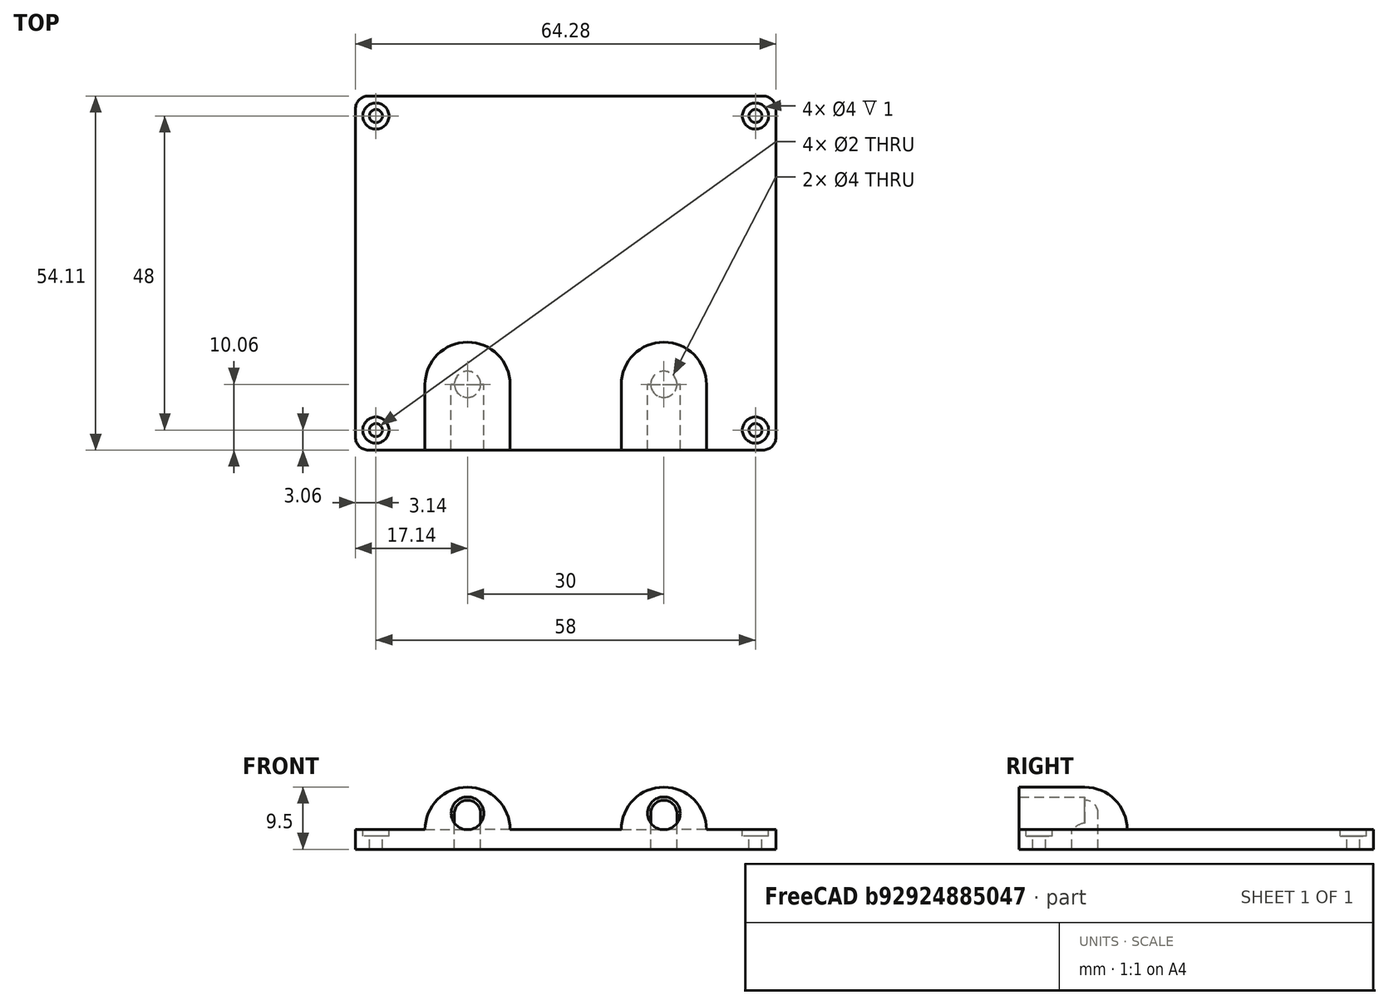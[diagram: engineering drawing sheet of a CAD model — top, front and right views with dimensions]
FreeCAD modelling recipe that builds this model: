
FCSTD DOCUMENT  (FreeCAD 0.19R24276 (Git))
Label: enclosureBack
License: All rights reserved
LicenseURL: http://en.wikipedia.org/wiki/All_rights_reserved
objects: Part::Cylinder×14, Part::MultiFuse×13, Part::Cut×4, Part::Sphere×4, Part::Box×3, Spreadsheet::Sheet×1, Part::Fillet×1
note: 39 computed .brp shape members not serialized (recipe doc carries the construction recipe); baked Part::Feature solids carry a one-line shape summary decoded from their .brp

FEATURE [Spreadsheet::Sheet] Spreadsheet  label="data"
  cells = A4=hole_dia; B4(hole_dia)==1.5mm; A5=standoff_dia; B5(standoff_dia)==4mm; A6=standoff_height; B6(standoff_height)==8mm; A7=case_standoff_dia; B7(case_standoff_dia)==5mm; A8=wall_thickness; B8(wall_thickness)==3mm; A9=case_thickness; B9(case_thickness)==15mm; A10=case_inner_width; B10(case_inner_width)==2.55in - 0.5mm; A11=case_inner_height; B11(case_inner_height)==2.15in - 0.5mm; A12=post_dia; B12(post_dia)==5mm; A13=post_depth; B13(post_depth)==10mm
FEATURE [Part::Box] Box  label="Cube"
  AttacherType = Attacher::AttachEngine3D
  Height = 3
  Length = 64.27
  Placement = pos=(-32.135,-27.055,0) rot=(0,0,1;0rad)
  Width = 54.11
  expr: Length = <<data>>.case_inner_width
  expr: Width = <<data>>.case_inner_height
  expr: .Placement.Base.y = -<<data>>.case_inner_height / 2
  expr: .Placement.Base.x = -<<data>>.case_inner_width / 2
  expr: Height = <<data>>.wall_thickness
FEATURE [Part::Fillet] Fillet
  Base = -> Box
  Edges = 4 edges r=2: [Edge1,Edge3,Edge5,Edge7]
FEATURE [Part::Cylinder] Cylinder
  Angle = 360
  AttacherType = Attacher::AttachEngine3D
  Height = 2
  Placement = pos=(0,0,2) rot=(0,0,1;0rad)
  Radius = 2
FEATURE [Part::Cylinder] Cylinder001
  Angle = 360
  AttacherType = Attacher::AttachEngine3D
  Height = 10
  Radius = 1
FEATURE [Part::MultiFuse] Fusion  label="screwHole"
  Placement = pos=(29,24,0) rot=(0,0,1;0rad)
  Shapes = -> [Cylinder001,Cylinder]
FEATURE [Part::Cylinder] Cylinder002
  Angle = 360
  AttacherType = Attacher::AttachEngine3D
  Height = 2
  Placement = pos=(0,0,2) rot=(0,0,1;0rad)
  Radius = 2
FEATURE [Part::Cylinder] Cylinder003
  Angle = 360
  AttacherType = Attacher::AttachEngine3D
  Height = 10
  Radius = 1
FEATURE [Part::MultiFuse] Fusion006  label="screwHole001"
  Placement = pos=(-29,24,0) rot=(0,0,1;0rad)
  Shapes = -> [Cylinder003,Cylinder002]
FEATURE [Part::Cylinder] Cylinder004
  Angle = 360
  AttacherType = Attacher::AttachEngine3D
  Height = 2
  Placement = pos=(0,0,2) rot=(0,0,1;0rad)
  Radius = 2
FEATURE [Part::Cylinder] Cylinder005
  Angle = 360
  AttacherType = Attacher::AttachEngine3D
  Height = 10
  Radius = 1
FEATURE [Part::MultiFuse] Fusion007  label="screwHole002"
  Placement = pos=(29,-24,0) rot=(0,0,1;0rad)
  Shapes = -> [Cylinder005,Cylinder004]
FEATURE [Part::Cylinder] Cylinder006
  Angle = 360
  AttacherType = Attacher::AttachEngine3D
  Height = 2
  Placement = pos=(0,0,2) rot=(0,0,1;0rad)
  Radius = 2
FEATURE [Part::Cylinder] Cylinder007
  Angle = 360
  AttacherType = Attacher::AttachEngine3D
  Height = 10
  Radius = 1
FEATURE [Part::MultiFuse] Fusion008  label="screwHole003"
  Placement = pos=(-29,-24,0) rot=(0,0,1;0rad)
  Shapes = -> [Cylinder007,Cylinder006]
FEATURE [Part::MultiFuse] Fusion009  label="ScrewHoles"
  Shapes = -> [Fusion008,Fusion,Fusion006,Fusion007]
FEATURE [Part::Cut] Cut
  Base = -> Fillet
  Tool = -> Fusion009
FEATURE [Part::Cylinder] Cylinder008
  Angle = 360
  AttacherType = Attacher::AttachEngine3D
  Height = 10
  Radius = 6.5
  expr: Height = <<data>>.post_depth
FEATURE [Part::Sphere] Sphere
  Angle1 = -90
  Angle2 = 90
  Angle3 = 360
  AttacherType = Attacher::AttachEngine3D
  Placement = pos=(0,0,10) rot=(0,0,1;0rad)
  Radius = 6.5
FEATURE [Part::Box] Box001  label="Cube001"
  AttacherType = Attacher::AttachEngine3D
  Height = 31
  Length = 16
  Placement = pos=(-8,0,0) rot=(0,0,1;0rad)
  Width = 10
FEATURE [Part::MultiFuse] Fusion010
  Shapes = -> [Sphere,Cylinder008]
FEATURE [Part::Cylinder] Cylinder009
  Angle = 360
  AttacherType = Attacher::AttachEngine3D
  Height = 10
  Placement = pos=(0,-2.5,0) rot=(0,0,1;0rad)
  Radius = 2.5
  expr: .Placement.Base.y = -<<data>>.post_dia / 2
  expr: Height = <<data>>.post_depth
  expr: Radius = <<data>>.post_dia / 2
FEATURE [Part::MultiFuse] Fusion011
  Shapes = -> [Cylinder009,Box001]
FEATURE [Part::Cut] Cut001  label="Hump"
  Base = -> Fusion010
  Placement = pos=(-15,-27.055,3) rot=(-1,0,0;1.5708rad)
  Tool = -> Fusion011
  expr: .Placement.Base.y = -<<data>>.case_inner_height / 2
  expr: .Placement.Base.z = <<data>>.wall_thickness
FEATURE [Part::Cylinder] Cylinder010
  Angle = 360
  AttacherType = Attacher::AttachEngine3D
  Height = 10
  Placement = pos=(0,-2.5,0) rot=(0,0,1;0rad)
  Radius = 2.5
  expr: Radius = <<data>>.post_dia / 2
  expr: Height = <<data>>.post_depth
  expr: .Placement.Base.y = -<<data>>.post_dia / 2
FEATURE [Part::Box] Box002  label="Cube002"
  AttacherType = Attacher::AttachEngine3D
  Height = 31
  Length = 16
  Placement = pos=(-8,0,0) rot=(0,0,1;0rad)
  Width = 10
FEATURE [Part::MultiFuse] Fusion012
  Shapes = -> [Cylinder010,Box002]
FEATURE [Part::Sphere] Sphere001
  Angle1 = -90
  Angle2 = 90
  Angle3 = 360
  AttacherType = Attacher::AttachEngine3D
  Placement = pos=(0,0,10) rot=(0,0,1;0rad)
  Radius = 6.5
FEATURE [Part::Cylinder] Cylinder011
  Angle = 360
  AttacherType = Attacher::AttachEngine3D
  Height = 10
  Radius = 6.5
  expr: Height = <<data>>.post_depth
FEATURE [Part::MultiFuse] Fusion013
  Shapes = -> [Sphere001,Cylinder011]
FEATURE [Part::Cut] Cut002  label="Hump001"
  Base = -> Fusion013
  Placement = pos=(15,-27.055,3) rot=(-1,0,0;1.5708rad)
  Tool = -> Fusion012
  expr: .Placement.Base.y = -<<data>>.case_inner_height / 2
  expr: .Placement.Base.z = <<data>>.wall_thickness
FEATURE [Part::Cylinder] Cylinder012
  Angle = 360
  AttacherType = Attacher::AttachEngine3D
  Height = 5.5
  Placement = pos=(-15,-17,0) rot=(0,0,1;0rad)
  Radius = 2
  expr: Radius = <<data>>.post_dia / 2 - 0.5mm
FEATURE [Part::MultiFuse] Fusion015
  Shapes = -> [Cut002,Cut001,Cut]
FEATURE [Part::Sphere] Sphere002
  Angle1 = -90
  Angle2 = 90
  Angle3 = 360
  AttacherType = Attacher::AttachEngine3D
  Placement = pos=(-15,-17,5.5) rot=(0,0,1;0rad)
  Radius = 2
  expr: Radius = <<data>>.post_dia / 2 - 0.5mm
FEATURE [Part::MultiFuse] Fusion016
  Shapes = -> [Sphere002,Cylinder012]
FEATURE [Part::Cylinder] Cylinder013
  Angle = 360
  AttacherType = Attacher::AttachEngine3D
  Height = 5.5
  Placement = pos=(-15,-17,0) rot=(0,0,1;0rad)
  Radius = 2
  expr: Radius = <<data>>.post_dia / 2 - 0.5mm
FEATURE [Part::Sphere] Sphere003
  Angle1 = -90
  Angle2 = 90
  Angle3 = 360
  AttacherType = Attacher::AttachEngine3D
  Placement = pos=(-15,-17,5.5) rot=(0,0,1;0rad)
  Radius = 2
  expr: Radius = <<data>>.post_dia / 2 - 0.5mm
FEATURE [Part::MultiFuse] Fusion017
  Placement = pos=(30,0,0) rot=(0,0,1;0rad)
  Shapes = -> [Sphere003,Cylinder013]
FEATURE [Part::MultiFuse] Fusion018
  Shapes = -> [Fusion017,Fusion016]
FEATURE [Part::Cut] Cut003  label="DisplayBack"
  Base = -> Fusion015
  Tool = -> Fusion018
